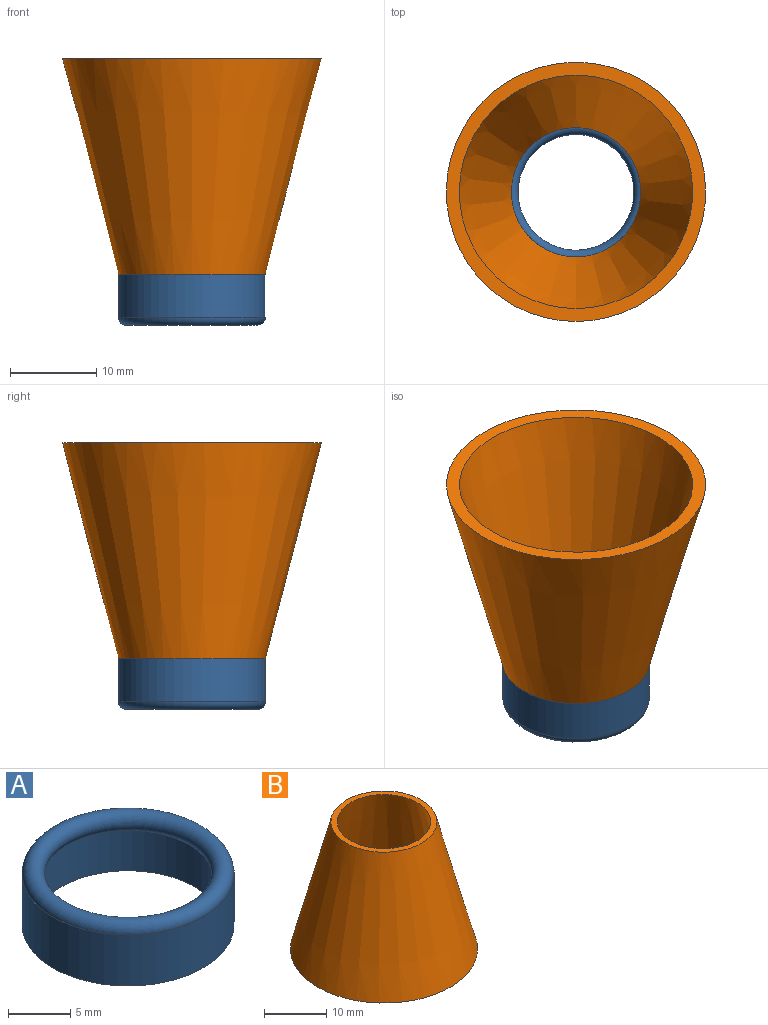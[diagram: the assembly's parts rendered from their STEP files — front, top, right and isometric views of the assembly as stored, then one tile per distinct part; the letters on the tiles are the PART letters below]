
ASSEMBLY  parts=2 mates=1
PART A: 5 faces, bbox 18.4x18.4x5.9 mm
  f0: torus R=7.59mm, axis (0,0,-1), area 191.9mm2, adj f1,f4
  f1: cylinder r=7.5mm len=15mm, axis (0,0,1), area 193.6mm2, adj f0,f3
  f2: cylinder r=8.5mm len=17mm, axis (0,0,1), area 267mm2, adj f3,f4
  f3: plane 17x17mm, normal (0,0,-1), area 50.3mm2, adj f1,f2
  f4: plane 17x17mm, normal (0,0,1), area 0.6mm2, adj f0,f2
PART B: 4 faces, bbox 30x30x25 mm
  f0: plane 17x17mm, normal (0,0,1), area 50.3mm2, adj f2,f3
  f1: plane 30x30mm, normal (0,0,-1), area 134.3mm2, adj f2,f3
  f2: cone r=8.5mm half-angle=14.6deg, axis (0,0,-1), area 1907mm2, adj f0,f1
  f3: cone r=13.5mm half-angle=13.5deg, axis (0,0,-1), area 1696.2mm2, adj f0,f1
PLACE A rot(axis=(0,1,0),180deg) t=(49.11,23.82,-18.87)mm fixed
PLACE B rot(axis=(0.71,0.71,0),180deg) t=(49.11,23.82,-18.87)mm
MATE fastened A.f2 <-> B.f2  axis (0,0,1) through (49.11,23.82,-13.87)mm
